# Revit family: Bathroom-Accessory-Waterworks-Flyte-Paper_Holder
name_source: partatom
category: Specialty Equipment
revit_build: Autodesk Revit MEP 2014 (Build: 20140709_2115(x64)
units: mm (PartAtom-declared; Revit-internal decimal feet)

## types (4) — shared parameters
Assembly Code = C1030200
Default Elevation = 3' - 0"
Depth = 0' - 3 7/16"
Height = 0' - 2 3/8"
Keynote = 22 40 00
Length = 0' - 7 3/4"
Manufacturer = Waterworks
Model = FLPH01
Product Documentation Link = http://assets.waterworks.com
Product Page URL = http://www.waterworks.com
URL = http://www.waterworks.com
Version = 2014 - v1.0a
Warranty = http://www.waterworks.com
‌Installation Requirements or Notes = Wall Mounted Installation

## per-type parameters (varying)
| type | Constraint | Description | Finish | Model SKU | Product Name |
| Chrome | 1 | Wall Mounted One Arm Paper Holder in Chrome | Metal - Waterworks - Chrome | 22-17622-62164 | Flyte Wall Mounted One Arm Paper Holder in Chrome |
| Graphite | 2 | Wall Mounted One Arm Paper Holder in Graphite | Metal - Waterworks - Graphite | 22-76729-62115 | Flyte Wall Mounted One Arm Paper Holder in Graphite |
| Nickel | 3 | Wall Mounted One Arm Paper Holder in Nickel | Metal - Waterworks - Nickel | 22-90528-33304 | Flyte Wall Mounted One Arm Paper Holder in Nickel |
| Unlacquered Brass | 4 | Wall Mounted One Arm Paper Holder in Unlacquered Brass | Metal - Waterworks - Unlacquered Brass | 22-18638-54642 | Flyte Wall Mounted One Arm Paper Holder in Unlacquered Brass |

## geometry (parser evidence)
native form markers: Sweep x6
no freeform markers — native parametric forms only
